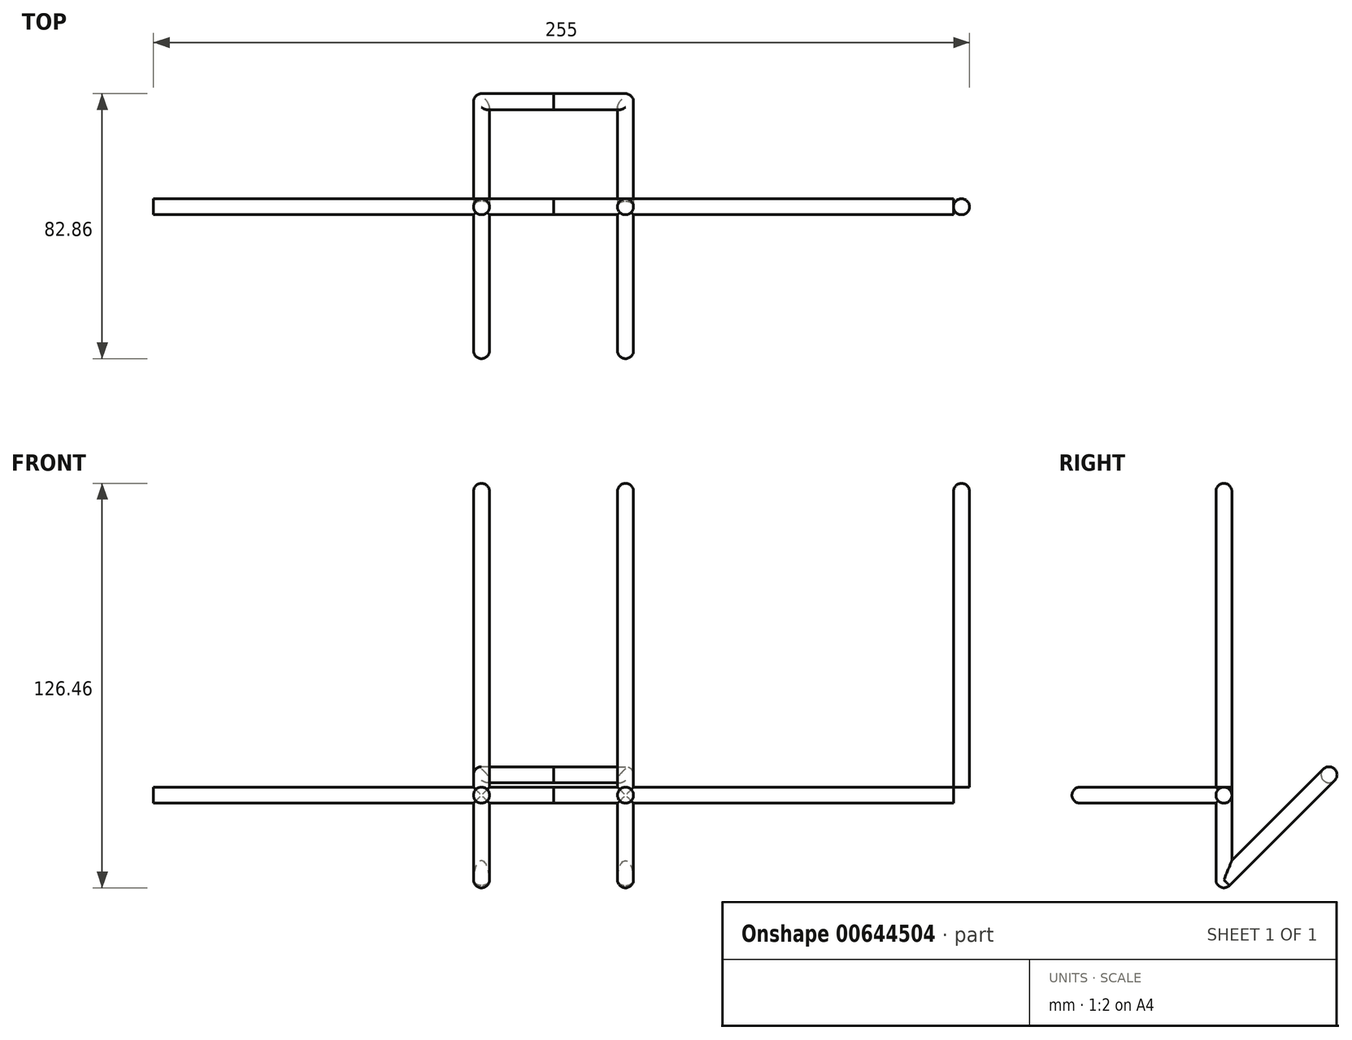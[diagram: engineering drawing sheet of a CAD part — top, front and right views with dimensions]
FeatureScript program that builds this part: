
annotation { "Feature Type Name" : "Feature", "Feature Type Description" : "" }
export const myFeature = defineFeature(function(context is Context, id is Id, definition is map)
    precondition{}
    {
        {
            assignVariable(context, id + "F0", {"name" : "d", "anyValue" : 5});
        }
        {
            var Q0;
            Q0=qCreatedBy(makeId("Front.planeOp"),FACE);
            var sketch = newSketch(context, id + "F1", { "sketchPlane" : qUnion([Q0])});
            skLineSegment(sketch, "E0.bottom", {"start": v(0, 0) * mm, "end": v(130, 0) * mm});
            skLineSegment(sketch, "E0.top", {"start": v(0, 5) * mm, "end": v(130, 5) * mm});
            skLineSegment(sketch, "E0.left", {"start": v(0, 0) * mm, "end": v(0, 5) * mm});
            skLineSegment(sketch, "E0.right", {"start": v(130, 0) * mm, "end": v(130, 5) * mm});
            skLineSegment(sketch, "E1.bottom", {"start": v(130, 0) * mm, "end": v(125, 0) * mm});
            skLineSegment(sketch, "E1.top", {"start": v(130, 100) * mm, "end": v(125, 100) * mm});
            skLineSegment(sketch, "E1.left", {"start": v(130, 0) * mm, "end": v(130, 100) * mm});
            skLineSegment(sketch, "E1.right", {"start": v(125, 0) * mm, "end": v(125, 100) * mm});
            skLineSegment(sketch, "E2.bottom", {"start": v(20, -25) * mm, "end": v(25, -25) * mm});
            skLineSegment(sketch, "E2.top", {"start": v(20, 100) * mm, "end": v(25, 100) * mm});
            skLineSegment(sketch, "E2.left", {"start": v(20, -25) * mm, "end": v(20, 100) * mm});
            skLineSegment(sketch, "E2.right", {"start": v(25, -25) * mm, "end": v(25, 100) * mm});
            skLineSegment(sketch, "E3", {"start": v(20, -17.93) * mm, "end": v(25, -17.93) * mm});
            skSolve(sketch);
        }
        {
            var Q0;
            {var subQ0=sQuery(id+"F1.wireOp",EDGE,"E0.left");Q0=makeQuery(id+"F1.imprint","IMPRINT",FACE,{"disambiguationData":[TD([[makeQuery(id+"F1.imprint","IMPRINT",EDGE,{"derivedFrom":subQ0}),-1.0]])]});}
            var Q1;
            {var subQ5=sQuery(id+"F1.wireOp",EDGE,"E2.top");Q1=makeQuery(id+"F1.imprint","IMPRINT",FACE,{"disambiguationData":[TD([[makeQuery(id+"F1.imprint","IMPRINT",EDGE,{"derivedFrom":subQ5}),-1.0]])]});}
            var Q2;
            {var subQ3=sQuery(id+"F1.wireOp",EDGE,"E2.right");var subQ5=sQuery(id+"F1.wireOp",EDGE,"E0.top");var subQ7=makeQuery(id+"F1.imprint","INTERSECT",VERTEX,{"derivedFrom":[subQ5,subQ3]});Q2=makeQuery(id+"F1.imprint","IMPRINT",FACE,{"disambiguationData":[TD([[makeQuery(id+"F1.imprint","IMPRINT",EDGE,{"disambiguationData":[TD([[subQ7,-1.0]])],"derivedFrom":subQ5}),-1.0]])]});}
            var Q3;
            {var subQ5=sQuery(id+"F1.wireOp",EDGE,"E1.top");Q3=makeQuery(id+"F1.imprint","IMPRINT",FACE,{"disambiguationData":[TD([[makeQuery(id+"F1.imprint","IMPRINT",EDGE,{"derivedFrom":subQ5}),1.0]])]});}
            var Q4;
            {var subQ5=sQuery(id+"F1.wireOp",EDGE,"E2.bottom");Q4=makeQuery(id+"F1.imprint","IMPRINT",FACE,{"disambiguationData":[TD([[makeQuery(id+"F1.imprint","IMPRINT",EDGE,{"derivedFrom":subQ5}),1.0]])]});}
            var Q5;
            {var subQ0=sQuery(id+"F1.wireOp",EDGE,"E2.left");var subQ1=sQuery(id+"F1.wireOp",EDGE,"E0.bottom");var subQ2=makeQuery(id+"F1.imprint","INTERSECT",VERTEX,{"derivedFrom":[subQ1,subQ0]});Q5=makeQuery(id+"F1.imprint","IMPRINT",FACE,{"disambiguationData":[TD([[makeQuery(id+"F1.imprint","IMPRINT",EDGE,{"disambiguationData":[TD([[subQ2,-1.0]])],"derivedFrom":subQ1}),1.0]])]});}
            var Q6;
            {var subQ5=sQuery(id+"F1.wireOp",EDGE,"E1.bottom");Q6=makeQuery(id+"F1.imprint","IMPRINT",FACE,{"disambiguationData":[TD([[makeQuery(id+"F1.imprint","IMPRINT",EDGE,{"derivedFrom":subQ5}),-1.0]])]});}
            var Q7;
            {var subQ5=sQuery(id+"F1.wireOp",EDGE,"E3");Q7=makeQuery(id+"F1.imprint","IMPRINT",FACE,{"disambiguationData":[TD([[makeQuery(id+"F1.imprint","IMPRINT",EDGE,{"derivedFrom":subQ5}),1.0]])]});}
            extrude(context, id + "F2", {"entities" : qUnion([Q0, Q1, Q2, Q3, Q4, Q5, Q6, Q7]), "depth" : (getVariable(context, 'd')) * mm, "offsetDistance" : 25 * mm});
        }
        {
            var Q0;
            {var subQ0=sQuery(id+"F1.wireOp",EDGE,"E2.left");var subQ1=sQuery(id+"F1.wireOp",EDGE,"E0.bottom");var subQ2=makeQuery(id+"F1.imprint","INTERSECT",VERTEX,{"derivedFrom":[subQ1,subQ0]});Q0=makeQuery(id+"F1.imprint","IMPRINT",FACE,{"disambiguationData":[TD([[makeQuery(id+"F1.imprint","IMPRINT",EDGE,{"disambiguationData":[TD([[subQ2,-1.0]])],"derivedFrom":subQ1}),1.0]])]});}
            var Q1;
            {var subQ5=sQuery(id+"F1.wireOp",EDGE,"E1.bottom");Q1=makeQuery(id+"F1.imprint","IMPRINT",FACE,{"disambiguationData":[TD([[makeQuery(id+"F1.imprint","IMPRINT",EDGE,{"derivedFrom":subQ5}),-1.0]])]});}
            extrude(context, id + "F3", {"entities" : qUnion([Q0, Q1]), "operationType" : NewBodyOperationType.ADD, "depth" : 50 * mm, "offsetDistance" : 25 * mm});
        }
        {
            var Q0;
            {var subQ0=sQuery(id+"F1.wireOp",EDGE,"E2.right");var subQ1=makeQuery(id+"F1.imprint","INTERSECT",VERTEX,{"derivedFrom":[subQ0,sQuery(id+"F1.wireOp",EDGE,"E3")]});Q0=makeQuery(id+"F7.opFillet","MERGE",FACE,{"derivedFrom":[makeQuery(id+"F2.opExtrude","SWEPT_FACE",FACE,{"disambiguationData":[OSD([subQ0]),TDD([makeQuery(id+"F1.imprint","IMPRINT",EDGE,{"disambiguationData":[TD([[makeQuery(id+"F1.imprint","INTERSECT",VERTEX,{"derivedFrom":[sQuery(id+"F1.wireOp",EDGE,"E2.top"),subQ0]}),1.0]])],"derivedFrom":subQ0})])]}),makeQuery(id+"F3.opExtrude","SWEPT_FACE",FACE,{"disambiguationData":[OSD([subQ0])]}),makeQuery(id+"FC98wvK5Y8fu9cm_1.boolean.opBoolean","MERGE",FACE,{"derivedFrom":[makeQuery(id+"F2.opExtrude","SWEPT_FACE",FACE,{"disambiguationData":[OSD([subQ0]),TDD([makeQuery(id+"F1.imprint","IMPRINT",EDGE,{"disambiguationData":[TD([[makeQuery(id+"F1.imprint","INTERSECT",VERTEX,{"derivedFrom":[sQuery(id+"F1.wireOp",EDGE,"E2.bottom"),subQ0]}),-1.0]])],"derivedFrom":subQ0}),makeQuery(id+"F1.imprint","IMPRINT",EDGE,{"disambiguationData":[TD([[subQ1,-1.0]])],"derivedFrom":subQ0})])]}),makeQuery(id+"FC98wvK5Y8fu9cm_1.opExtrude","SWEPT_FACE",FACE,{"disambiguationData":[OSD([subQ0])]})]})]});}
            var sketch = newSketch(context, id + "F4", { "sketchPlane" : qUnion([Q0])});
            skLineSegment(sketch, "E4", {"start": v(-5, -22.93) * mm, "end": v(30.36, 12.43) * mm});
            skLineSegment(sketch, "E5.bottom", {"start": v(30.36, 12.43) * mm, "end": v(33.9, 8.9) * mm});
            skLineSegment(sketch, "E5.top", {"start": v(26.82, 8.9) * mm, "end": v(30.36, 5.36) * mm});
            skLineSegment(sketch, "E5.left", {"start": v(30.36, 12.43) * mm, "end": v(26.82, 8.9) * mm});
            skLineSegment(sketch, "E5.right", {"start": v(33.9, 8.9) * mm, "end": v(30.36, 5.36) * mm});
            skSolve(sketch);
        }
        {
            var Q0;
            {var subQ0=sQuery(id+"F1.wireOp",EDGE,"E2.bottom");Q0=makeQuery(id+"F1.imprint","IMPRINT",FACE,{"disambiguationData":[TD([[makeQuery(id+"F1.imprint","IMPRINT",EDGE,{"derivedFrom":subQ0}),1.0]])]});}
            var Q1;
            Q1=sQuery(id+"F4.wireOp",EDGE,"E4");
            sweep(context, id + "F5", {"operationType" : NewBodyOperationType.ADD, "profiles" : qUnion([Q0]), "path" : qUnion([Q1])});
        }
        {
            var Q0;
            Q0=makeQuery(id+"F4.imprint","IMPRINT",FACE,{"disambiguationData":[TD([[makeQuery(id+"F4.imprint","IMPRINT",EDGE,{"derivedFrom":sQuery(id+"F4.wireOp",EDGE,"E5.bottom")}),-1.0]])]});
            var Q1;
            Q1=makeQuery(id+"F2.opExtrude","SWEPT_FACE",FACE,{"disambiguationData":[OSD([sQuery(id+"F1.wireOp",EDGE,"E0.left")])]});
            extrude(context, id + "F6", {"entities" : qUnion([Q0]), "operationType" : NewBodyOperationType.ADD, "endBound" : BoundingType.UP_TO_SURFACE, "oppositeDirection" : true, "depth" : 25 * mm, "endBoundEntityFace" : qUnion([Q1]), "offsetDistance" : 25 * mm});
        }
        {
            var Q0;
            {var subQ0=sQuery(id+"F1.wireOp",EDGE,"E0.top");Q0=makeQuery(id+"F2.opExtrude","CAP_EDGE",EDGE,{"disambiguationData":[OSD([subQ0]),TDD([makeQuery(id+"F1.imprint","IMPRINT",EDGE,{"disambiguationData":[TD([[makeQuery(id+"F1.imprint","INTERSECT",VERTEX,{"derivedFrom":[subQ0,sQuery(id+"F1.wireOp",EDGE,"E2.right")]}),-1.0]])],"derivedFrom":subQ0})])],"isStart":false});}
            var Q1;
            Q1=makeQuery(id+"F2.opExtrude","CAP_EDGE",EDGE,{"disambiguationData":[OSD([sQuery(id+"F1.wireOp",EDGE,"E0.bottom"),sQuery(id+"F1.wireOp",EDGE,"E1.bottom")])],"isStart":false});
            var Q2;
            Q2=makeQuery(id+"F2.opExtrude","CAP_EDGE",EDGE,{"disambiguationData":[OSD([sQuery(id+"F1.wireOp",EDGE,"E0.bottom"),sQuery(id+"F1.wireOp",EDGE,"E1.bottom")])],"isStart":true});
            var Q3;
            {var subQ0=sQuery(id+"F1.wireOp",EDGE,"E0.top");Q3=makeQuery(id+"F2.opExtrude","CAP_EDGE",EDGE,{"disambiguationData":[OSD([subQ0]),TDD([makeQuery(id+"F1.imprint","IMPRINT",EDGE,{"disambiguationData":[TD([[makeQuery(id+"F1.imprint","INTERSECT",VERTEX,{"derivedFrom":[subQ0,sQuery(id+"F1.wireOp",EDGE,"E2.right")]}),-1.0]])],"derivedFrom":subQ0})])],"isStart":true});}
            var Q4;
            Q4=makeQuery(id+"F2.opExtrude","CAP_EDGE",EDGE,{"disambiguationData":[OSD([sQuery(id+"F1.wireOp",EDGE,"E0.bottom")])],"isStart":true});
            var Q5;
            {var subQ0=sQuery(id+"F1.wireOp",EDGE,"E0.top");Q5=makeQuery(id+"F2.opExtrude","CAP_EDGE",EDGE,{"disambiguationData":[OSD([subQ0]),TDD([makeQuery(id+"F1.imprint","IMPRINT",EDGE,{"disambiguationData":[TD([[makeQuery(id+"F1.imprint","INTERSECT",VERTEX,{"derivedFrom":[subQ0,sQuery(id+"F1.wireOp",EDGE,"E0.left")]}),-1.0]])],"derivedFrom":subQ0})])],"isStart":true});}
            var Q6;
            {var subQ0=sQuery(id+"F1.wireOp",EDGE,"E0.top");Q6=makeQuery(id+"F2.opExtrude","CAP_EDGE",EDGE,{"disambiguationData":[OSD([subQ0]),TDD([makeQuery(id+"F1.imprint","IMPRINT",EDGE,{"disambiguationData":[TD([[makeQuery(id+"F1.imprint","INTERSECT",VERTEX,{"derivedFrom":[subQ0,sQuery(id+"F1.wireOp",EDGE,"E0.left")]}),-1.0]])],"derivedFrom":subQ0})])],"isStart":false});}
            var Q7;
            Q7=makeQuery(id+"F2.opExtrude","CAP_EDGE",EDGE,{"disambiguationData":[OSD([sQuery(id+"F1.wireOp",EDGE,"E0.bottom")])],"isStart":false});
            fillet(context, id + "F7", {"entities" : qUnion([Q0, Q1, Q2, Q3, Q4, Q5, Q6, Q7]), "radius" : (.5 * getVariable(context, 'd')) * mm, "tangentPropagation" : true, "allowEdgeOverflow" : false});
        }
        {
            var Q0;
            Q0=makeQuery(id+"F3.opExtrude","SWEPT_EDGE",EDGE,{"disambiguationData":[OSD([sQuery(id+"F1.wireOp",EDGE,"E0.top"),sQuery(id+"F1.wireOp",EDGE,"E2.right")])]});
            var Q1;
            Q1=makeQuery(id+"F3.opExtrude","SWEPT_EDGE",EDGE,{"disambiguationData":[OSD([sQuery(id+"F1.wireOp",EDGE,"E0.bottom"),sQuery(id+"F1.wireOp",EDGE,"E2.right")])]});
            var Q2;
            Q2=makeQuery(id+"F3.opExtrude","SWEPT_EDGE",EDGE,{"disambiguationData":[OSD([sQuery(id+"F1.wireOp",EDGE,"E0.top"),sQuery(id+"F1.wireOp",EDGE,"E2.left")])]});
            var Q3;
            Q3=makeQuery(id+"F3.opExtrude","SWEPT_EDGE",EDGE,{"disambiguationData":[OSD([sQuery(id+"F1.wireOp",EDGE,"E0.bottom"),sQuery(id+"F1.wireOp",EDGE,"E2.left")])]});
            var Q4;
            Q4=makeQuery(id+"F3.opExtrude","SWEPT_EDGE",EDGE,{"disambiguationData":[OSD([sQuery(id+"F1.wireOp",EDGE,"E0.top"),sQuery(id+"F1.wireOp",EDGE,"E1.left")])]});
            var Q5;
            Q5=makeQuery(id+"F3.opExtrude","SWEPT_EDGE",EDGE,{"disambiguationData":[OSD([sQuery(id+"F1.wireOp",EDGE,"E0.top"),sQuery(id+"F1.wireOp",EDGE,"E1.right")])]});
            var Q6;
            {var subQ0=sQuery(id+"F1.wireOp",EDGE,"E1.left");var subQ1=sQuery(id+"F1.wireOp",EDGE,"E1.bottom");Q6=makeQuery(id+"F3.boolean.opBoolean","MERGE",EDGE,{"derivedFrom":[makeQuery(id+"F2.opExtrude","SWEPT_EDGE",EDGE,{"disambiguationData":[OSD([subQ1,subQ0])]}),makeQuery(id+"F3.opExtrude","SWEPT_EDGE",EDGE,{"disambiguationData":[OSD([subQ1,subQ0])]})]});}
            var Q7;
            Q7=makeQuery(id+"F3.opExtrude","SWEPT_EDGE",EDGE,{"disambiguationData":[OSD([sQuery(id+"F1.wireOp",EDGE,"E0.bottom"),sQuery(id+"F1.wireOp",EDGE,"E1.bottom"),sQuery(id+"F1.wireOp",EDGE,"E1.right")])]});
            var Q8;
            Q8=makeQuery(id+"F6.boolean.opBoolean","MERGE",EDGE,{"derivedFrom":[makeQuery(id+"F5.opSweep","SWEPT_EDGE",EDGE,{"disambiguationData":[OSD([sQuery(id+"F1.wireOp",EDGE,"E2.bottom"),sQuery(id+"F1.wireOp",EDGE,"E2.right"),sQuery(id+"F4.wireOp",EDGE,"E4")])]}),makeQuery(id+"F6.opExtrude","CAP_EDGE",EDGE,{"disambiguationData":[OSD([sQuery(id+"F4.wireOp",EDGE,"E5.right")])],"isStart":true})]});
            var Q9;
            Q9=makeQuery(id+"F5.opSweep","SWEPT_EDGE",EDGE,{"disambiguationData":[OSD([sQuery(id+"F1.wireOp",EDGE,"E2.right"),sQuery(id+"F1.wireOp",EDGE,"E3"),sQuery(id+"F4.wireOp",EDGE,"E4")])]});
            var Q10;
            Q10=makeQuery(id+"F5.opSweep","SWEPT_EDGE",EDGE,{"disambiguationData":[OSD([sQuery(id+"F1.wireOp",EDGE,"E2.left"),sQuery(id+"F1.wireOp",EDGE,"E3"),sQuery(id+"F4.wireOp",EDGE,"E4")])]});
            var Q11;
            Q11=makeQuery(id+"F5.opSweep","SWEPT_EDGE",EDGE,{"disambiguationData":[OSD([sQuery(id+"F1.wireOp",EDGE,"E2.bottom"),sQuery(id+"F1.wireOp",EDGE,"E2.left"),sQuery(id+"F4.wireOp",EDGE,"E4")])]});
            var Q12;
            Q12=makeQuery(id+"F6.opExtrude","SWEPT_EDGE",EDGE,{"disambiguationData":[OSD([sQuery(id+"F4.wireOp",EDGE,"E5.top"),sQuery(id+"F4.wireOp",EDGE,"E5.left")])]});
            var Q13;
            Q13=makeQuery(id+"F6.opExtrude","SWEPT_EDGE",EDGE,{"disambiguationData":[OSD([sQuery(id+"F4.wireOp",EDGE,"E5.top"),sQuery(id+"F4.wireOp",EDGE,"E5.right")])]});
            var Q14;
            Q14=makeQuery(id+"F6.boolean.opBoolean","MERGE",EDGE,{"derivedFrom":[makeQuery(id+"F5.opSweep","CAP_EDGE",EDGE,{"disambiguationData":[OSD([sQuery(id+"F1.wireOp",EDGE,"E3"),sQuery(id+"F4.wireOp",VERTEX,"E4.end")])],"isStart":true}),makeQuery(id+"F6.opExtrude","SWEPT_EDGE",EDGE,{"disambiguationData":[OSD([sQuery(id+"F4.wireOp",EDGE,"E5.bottom"),sQuery(id+"F4.wireOp",EDGE,"E5.left")])]})]});
            var Q15;
            Q15=makeQuery(id+"F6.opExtrude","SWEPT_EDGE",EDGE,{"disambiguationData":[OSD([sQuery(id+"F4.wireOp",EDGE,"E5.bottom"),sQuery(id+"F4.wireOp",EDGE,"E5.right")])]});
            var Q16;
            Q16=makeQuery(id+"F6.opExtrude","CAP_EDGE",EDGE,{"disambiguationData":[OSD([sQuery(id+"F4.wireOp",EDGE,"E5.bottom")])],"isStart":true});
            var Q17;
            Q17=makeQuery(id+"F3.opExtrude","CAP_FACE",FACE,{"disambiguationData":[OSD([sQuery(id+"F1.wireOp",EDGE,"E0.bottom"),sQuery(id+"F1.wireOp",EDGE,"E0.top"),sQuery(id+"F1.wireOp",EDGE,"E2.left"),sQuery(id+"F1.wireOp",EDGE,"E2.right")])],"isStart":false});
            var Q18;
            Q18=makeQuery(id+"F3.opExtrude","CAP_FACE",FACE,{"disambiguationData":[OSD([sQuery(id+"F1.wireOp",EDGE,"E0.top"),sQuery(id+"F1.wireOp",EDGE,"E1.bottom"),sQuery(id+"F1.wireOp",EDGE,"E1.left"),sQuery(id+"F1.wireOp",EDGE,"E1.right")])],"isStart":false});
            fillet(context, id + "F8", {"entities" : qUnion([Q0, Q1, Q2, Q3, Q4, Q5, Q6, Q7, Q8, Q9, Q10, Q11, Q12, Q13, Q14, Q15, Q16, Q17, Q18]), "radius" : (.5 * getVariable(context, 'd')) * mm, "tangentPropagation" : true, "allowEdgeOverflow" : false});
        }
        {
            var Q0;
            Q0=makeQuery(id+"F2.opExtrude","CAP_EDGE",EDGE,{"disambiguationData":[OSD([sQuery(id+"F1.wireOp",EDGE,"E1.left")])],"isStart":false});
            var Q1;
            Q1=makeQuery(id+"F2.opExtrude","CAP_EDGE",EDGE,{"disambiguationData":[OSD([sQuery(id+"F1.wireOp",EDGE,"E1.right")])],"isStart":false});
            var Q2;
            Q2=makeQuery(id+"F2.opExtrude","CAP_EDGE",EDGE,{"disambiguationData":[OSD([sQuery(id+"F1.wireOp",EDGE,"E1.right")])],"isStart":true});
            var Q3;
            {var subQ0=sQuery(id+"F1.wireOp",EDGE,"E2.right");Q3=makeQuery(id+"F2.opExtrude","CAP_EDGE",EDGE,{"disambiguationData":[OSD([subQ0]),TDD([makeQuery(id+"F1.imprint","IMPRINT",EDGE,{"disambiguationData":[TD([[makeQuery(id+"F1.imprint","INTERSECT",VERTEX,{"derivedFrom":[sQuery(id+"F1.wireOp",EDGE,"E2.top"),subQ0]}),1.0]])],"derivedFrom":subQ0})])],"isStart":false});}
            var Q4;
            {var subQ0=sQuery(id+"F1.wireOp",EDGE,"E2.right");Q4=makeQuery(id+"F2.opExtrude","CAP_EDGE",EDGE,{"disambiguationData":[OSD([subQ0]),TDD([makeQuery(id+"F1.imprint","IMPRINT",EDGE,{"disambiguationData":[TD([[makeQuery(id+"F1.imprint","INTERSECT",VERTEX,{"derivedFrom":[sQuery(id+"F1.wireOp",EDGE,"E2.top"),subQ0]}),1.0]])],"derivedFrom":subQ0})])],"isStart":true});}
            var Q5;
            {var subQ0=sQuery(id+"F1.wireOp",EDGE,"E2.left");Q5=makeQuery(id+"F2.opExtrude","CAP_EDGE",EDGE,{"disambiguationData":[OSD([subQ0]),TDD([makeQuery(id+"F1.imprint","IMPRINT",EDGE,{"disambiguationData":[TD([[makeQuery(id+"F1.imprint","INTERSECT",VERTEX,{"derivedFrom":[sQuery(id+"F1.wireOp",EDGE,"E2.top"),subQ0]}),1.0]])],"derivedFrom":subQ0})])],"isStart":true});}
            var Q6;
            {var subQ0=sQuery(id+"F1.wireOp",EDGE,"E2.left");Q6=makeQuery(id+"F2.opExtrude","CAP_EDGE",EDGE,{"disambiguationData":[OSD([subQ0]),TDD([makeQuery(id+"F1.imprint","IMPRINT",EDGE,{"disambiguationData":[TD([[makeQuery(id+"F1.imprint","INTERSECT",VERTEX,{"derivedFrom":[sQuery(id+"F1.wireOp",EDGE,"E2.top"),subQ0]}),1.0]])],"derivedFrom":subQ0})])],"isStart":false});}
            var Q7;
            {var subQ0=sQuery(id+"F1.wireOp",EDGE,"E2.left");var subQ1=makeQuery(id+"F1.imprint","INTERSECT",VERTEX,{"derivedFrom":[subQ0,sQuery(id+"F1.wireOp",EDGE,"E3")]});Q7=makeQuery(id+"F5.boolean.opBoolean","MERGE",EDGE,{"derivedFrom":[makeQuery(id+"F2.opExtrude","CAP_EDGE",EDGE,{"disambiguationData":[OSD([subQ0]),TDD([makeQuery(id+"F1.imprint","IMPRINT",EDGE,{"disambiguationData":[TD([[makeQuery(id+"F1.imprint","INTERSECT",VERTEX,{"derivedFrom":[sQuery(id+"F1.wireOp",EDGE,"E2.bottom"),subQ0]}),-1.0]])],"derivedFrom":subQ0}),makeQuery(id+"F1.imprint","IMPRINT",EDGE,{"disambiguationData":[TD([[subQ1,-1.0]])],"derivedFrom":subQ0})])],"isStart":false}),makeQuery(id+"F5.opSweep","CAP_EDGE",EDGE,{"disambiguationData":[OSD([subQ0,sQuery(id+"F4.wireOp",VERTEX,"E4.start")])],"isStart":false})]});}
            var Q8;
            {var subQ0=sQuery(id+"F1.wireOp",EDGE,"E2.right");var subQ1=makeQuery(id+"F1.imprint","INTERSECT",VERTEX,{"derivedFrom":[subQ0,sQuery(id+"F1.wireOp",EDGE,"E3")]});Q8=makeQuery(id+"F5.boolean.opBoolean","MERGE",EDGE,{"derivedFrom":[makeQuery(id+"F2.opExtrude","CAP_EDGE",EDGE,{"disambiguationData":[OSD([subQ0]),TDD([makeQuery(id+"F1.imprint","IMPRINT",EDGE,{"disambiguationData":[TD([[makeQuery(id+"F1.imprint","INTERSECT",VERTEX,{"derivedFrom":[sQuery(id+"F1.wireOp",EDGE,"E2.bottom"),subQ0]}),-1.0]])],"derivedFrom":subQ0}),makeQuery(id+"F1.imprint","IMPRINT",EDGE,{"disambiguationData":[TD([[subQ1,-1.0]])],"derivedFrom":subQ0})])],"isStart":false}),makeQuery(id+"F5.opSweep","CAP_EDGE",EDGE,{"disambiguationData":[OSD([subQ0,sQuery(id+"F4.wireOp",VERTEX,"E4.start")])],"isStart":false})]});}
            var Q9;
            Q9=makeQuery(id+"F2.opExtrude","SWEPT_FACE",FACE,{"disambiguationData":[OSD([sQuery(id+"F1.wireOp",EDGE,"E1.top")])]});
            var Q10;
            Q10=makeQuery(id+"F2.opExtrude","SWEPT_FACE",FACE,{"disambiguationData":[OSD([sQuery(id+"F1.wireOp",EDGE,"E2.top")])]});
            fillet(context, id + "F9", {"entities" : qUnion([Q0, Q1, Q2, Q3, Q4, Q5, Q6, Q7, Q8, Q9, Q10]), "radius" : (.5 * getVariable(context, 'd')) * mm, "tangentPropagation" : true, "allowEdgeOverflow" : false});
        }
        {
            var Q0;
            Q0=makeQuery(id+"F2.opExtrude","SWEPT_BODY",BODY,{"disambiguationData":[OSD([sQuery(id+"F1.wireOp",EDGE,"E0.bottom"),sQuery(id+"F1.wireOp",EDGE,"E0.top"),sQuery(id+"F1.wireOp",EDGE,"E0.left"),sQuery(id+"F1.wireOp",EDGE,"E1.bottom"),sQuery(id+"F1.wireOp",EDGE,"E1.top"),sQuery(id+"F1.wireOp",EDGE,"E1.left"),sQuery(id+"F1.wireOp",EDGE,"E1.right"),sQuery(id+"F1.wireOp",EDGE,"E2.bottom"),sQuery(id+"F1.wireOp",EDGE,"E2.top"),sQuery(id+"F1.wireOp",EDGE,"E2.left"),sQuery(id+"F1.wireOp",EDGE,"E2.right")])]});
            var Q1;
            Q1=makeQuery(id+"F2.opExtrude","SWEPT_FACE",FACE,{"disambiguationData":[OSD([sQuery(id+"F1.wireOp",EDGE,"E0.left")])]});
            mirror(context, id + "F10", {"operationType" : NewBodyOperationType.ADD, "entities" : qUnion([Q0]), "mirrorPlane" : qUnion([Q1])});
        }
    });
